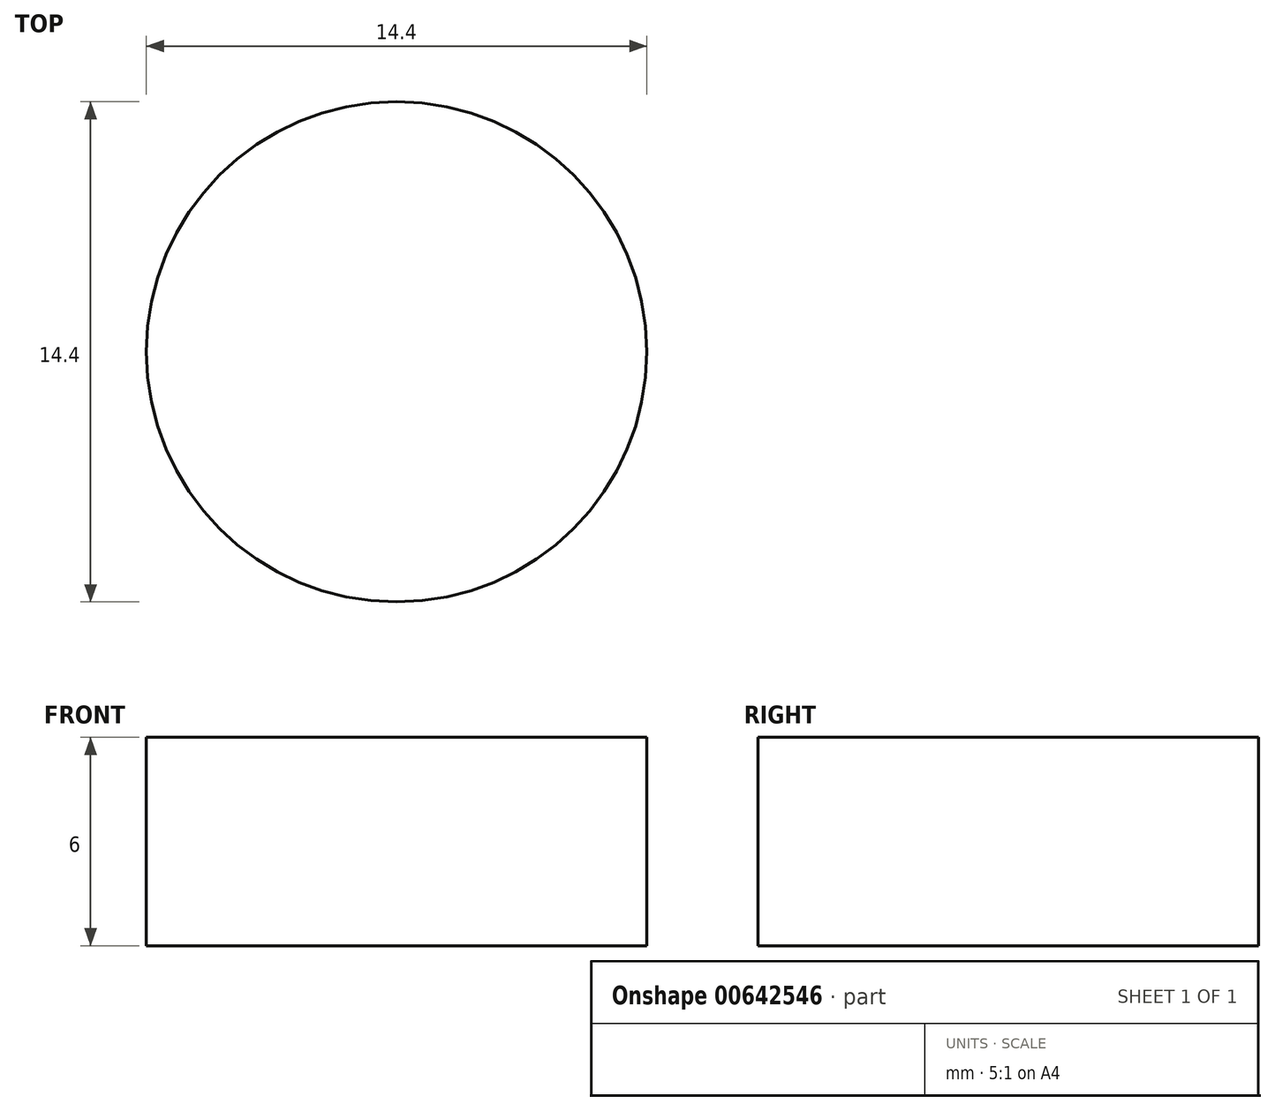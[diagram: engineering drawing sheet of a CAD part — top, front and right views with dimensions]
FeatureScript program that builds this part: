
annotation { "Feature Type Name" : "Feature", "Feature Type Description" : "" }
export const myFeature = defineFeature(function(context is Context, id is Id, definition is map)
    precondition{}
    {
        {
            var Q0;
            Q0=qCreatedBy(makeId("Top.planeOp"),FACE);
            var sketch = newSketch(context, id + "F0", { "sketchPlane" : qUnion([Q0])});
            skCircle(sketch, "E0", {"center": v(0, 0) * mm, "radius": 7.2 * mm});
            skSolve(sketch);
        }
        {
            var Q0;
            Q0=makeQuery(id+"F0.imprint","IMPRINT",FACE,{"disambiguationData":[TD([[makeQuery(id+"F0.imprint","IMPRINT",EDGE,{"derivedFrom":sQuery(id+"F0.wireOp",EDGE,"E0")}),1.0]])]});
            extrude(context, id + "F1", {"entities" : qUnion([Q0]), "depth" : 6 * mm, "offsetDistance" : 25.4 * mm});
        }
    });
